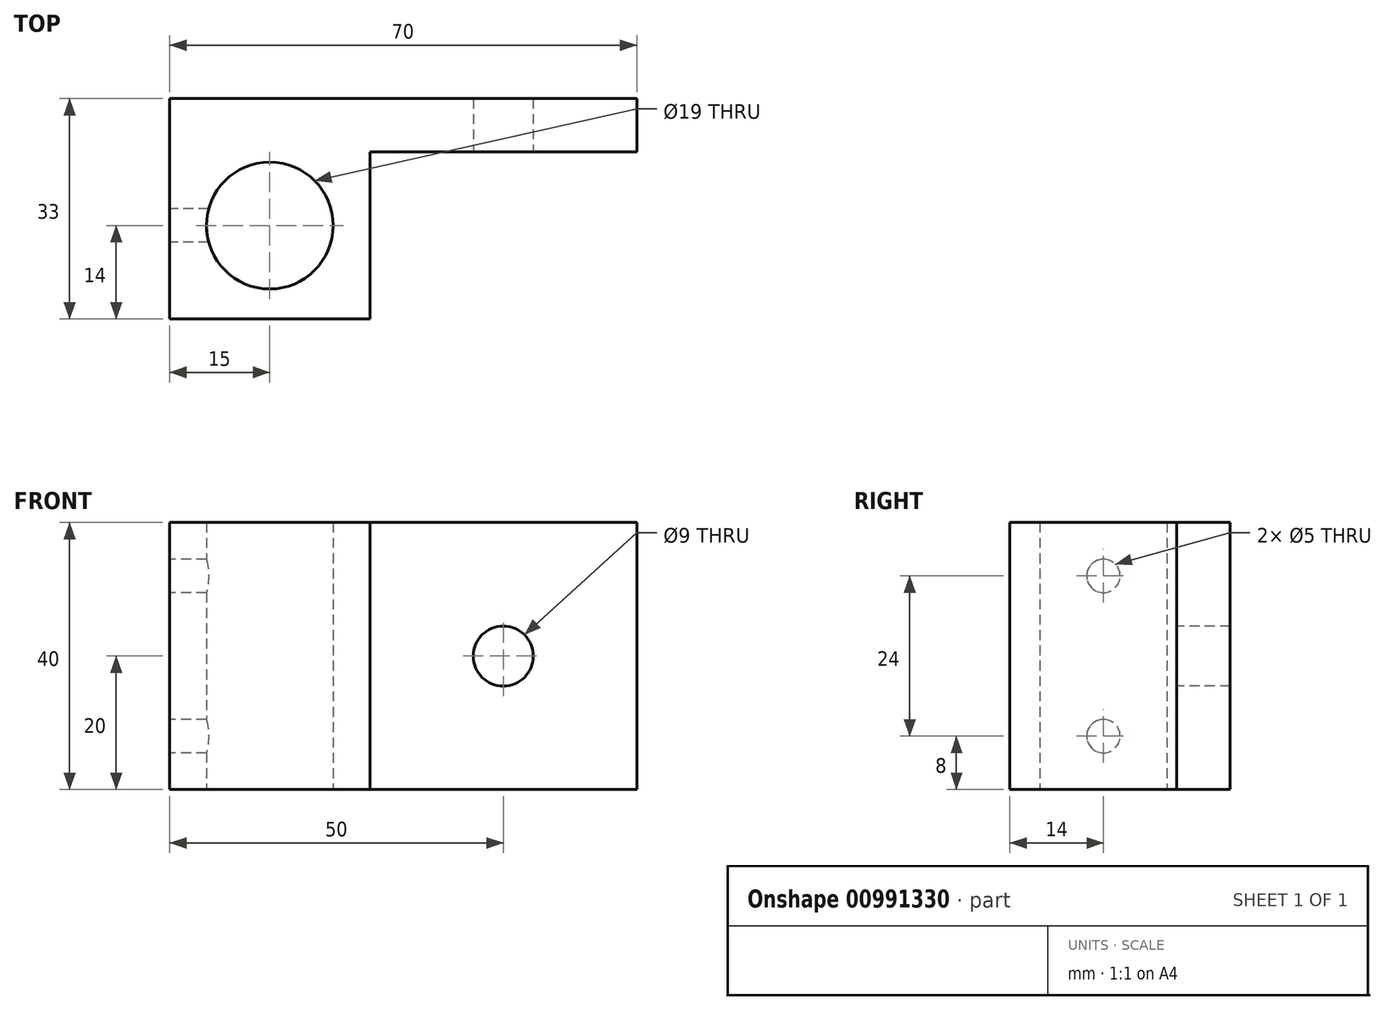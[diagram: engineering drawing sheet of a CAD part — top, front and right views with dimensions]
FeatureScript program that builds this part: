
annotation { "Feature Type Name" : "Feature", "Feature Type Description" : "" }
export const myFeature = defineFeature(function(context is Context, id is Id, definition is map)
    precondition{}
    {
        {
            var Q0;
            Q0=qCreatedBy(makeId("Front.planeOp"),FACE);
            var sketch = newSketch(context, id + "F0", { "sketchPlane" : qUnion([Q0])});
            skLineSegment(sketch, "E0.bottom", {"start": v(0, 0) * mm, "end": v(70, 0) * mm});
            skLineSegment(sketch, "E0.top", {"start": v(0, 40) * mm, "end": v(70, 40) * mm});
            skLineSegment(sketch, "E0.left", {"start": v(0, 0) * mm, "end": v(0, 40) * mm});
            skLineSegment(sketch, "E0.right", {"start": v(70, 0) * mm, "end": v(70, 40) * mm});
            skSolve(sketch);
        }
        {
            var Q0;
            Q0=makeQuery(id+"F0.imprint","IMPRINT",FACE,{"disambiguationData":[TD([[makeQuery(id+"F0.imprint","IMPRINT",EDGE,{"derivedFrom":sQuery(id+"F0.wireOp",EDGE,"E0.bottom")}),1.0]])]});
            extrude(context, id + "F1", {"entities" : qUnion([Q0]), "depth" : 8 * mm, "offsetDistance" : 25 * mm});
        }
        {
            var Q0;
            Q0=makeQuery(id+"F1.opExtrude","CAP_FACE",FACE,{"disambiguationData":[OSD([sQuery(id+"F0.wireOp",EDGE,"E0.bottom"),sQuery(id+"F0.wireOp",EDGE,"E0.top"),sQuery(id+"F0.wireOp",EDGE,"E0.left"),sQuery(id+"F0.wireOp",EDGE,"E0.right")])],"isStart":false});
            var sketch = newSketch(context, id + "F2", { "sketchPlane" : qUnion([Q0])});
            skLineSegment(sketch, "E1.bottom", {"start": v(0, 0) * mm, "end": v(30, 0) * mm});
            skLineSegment(sketch, "E1.top", {"start": v(0, 40) * mm, "end": v(30, 40) * mm});
            skLineSegment(sketch, "E1.left", {"start": v(0, 0) * mm, "end": v(0, 40) * mm});
            skLineSegment(sketch, "E1.right", {"start": v(30, 0) * mm, "end": v(30, 40) * mm});
            skSolve(sketch);
        }
        {
            var Q0;
            Q0=makeQuery(id+"F2.imprint","IMPRINT",FACE,{"disambiguationData":[TD([[makeQuery(id+"F2.imprint","IMPRINT",EDGE,{"derivedFrom":sQuery(id+"F2.wireOp",EDGE,"E1.bottom")}),1.0]])]});
            extrude(context, id + "F3", {"entities" : qUnion([Q0]), "operationType" : NewBodyOperationType.ADD, "depth" : 25 * mm, "offsetDistance" : 25 * mm});
        }
        {
            var Q0;
            Q0=makeQuery(id+"F3.boolean.opBoolean","MERGE",FACE,{"derivedFrom":[makeQuery(id+"F1.opExtrude","SWEPT_FACE",FACE,{"disambiguationData":[OSD([sQuery(id+"F0.wireOp",EDGE,"E0.bottom")])]}),makeQuery(id+"F3.opExtrude","SWEPT_FACE",FACE,{"disambiguationData":[OSD([sQuery(id+"F2.wireOp",EDGE,"E1.bottom")])]})]});
            var sketch = newSketch(context, id + "F4", { "sketchPlane" : qUnion([Q0])});
            skPoint(sketch, "E2", {"position": v(15, 19) * mm});
            skPoint(sketch, "E2.positionSnap1", {"position": v(15, 33) * mm});
            skCircle(sketch, "E3", {"center": v(15, 19) * mm, "radius": 9.5 * mm});
            skSolve(sketch);
        }
        {
            var Q0;
            Q0=makeQuery(id+"F4.imprint","IMPRINT",FACE,{"disambiguationData":[TD([[makeQuery(id+"F4.imprint","IMPRINT",EDGE,{"derivedFrom":sQuery(id+"F4.wireOp",EDGE,"E3")}),1.0]])]});
            extrude(context, id + "F5", {"entities" : qUnion([Q0]), "operationType" : NewBodyOperationType.REMOVE, "oppositeDirection" : true, "depth" : 40 * mm, "offsetDistance" : 25 * mm});
        }
        {
            var Q0;
            Q0=makeQuery(id+"F3.boolean.opBoolean","MERGE",FACE,{"derivedFrom":[makeQuery(id+"F1.opExtrude","SWEPT_FACE",FACE,{"disambiguationData":[OSD([sQuery(id+"F0.wireOp",EDGE,"E0.left")])]}),makeQuery(id+"F3.opExtrude","SWEPT_FACE",FACE,{"disambiguationData":[OSD([sQuery(id+"F2.wireOp",EDGE,"E1.left")])]})]});
            var sketch = newSketch(context, id + "F6", { "sketchPlane" : qUnion([Q0])});
            skPoint(sketch, "E4", {"position": v(33, 20) * mm});
            skPoint(sketch, "E5", {"position": v(19, 32) * mm});
            skPoint(sketch, "E6", {"position": v(19, 8) * mm});
            skSolve(sketch);
        }
        {
            var Q0;
            Q0=sQuery(id+"F6.wireOp",VERTEX,"E5");
            var Q1;
            Q1=sQuery(id+"F6.wireOp",VERTEX,"E6");
            var Q2;
            Q2=makeQuery(id+"F1.opExtrude","SWEPT_BODY",BODY,{"disambiguationData":[OSD([sQuery(id+"F0.wireOp",EDGE,"E0.bottom"),sQuery(id+"F0.wireOp",EDGE,"E0.top"),sQuery(id+"F0.wireOp",EDGE,"E0.left"),sQuery(id+"F0.wireOp",EDGE,"E0.right")])]});
            hole(context, id + "F7", {"style" : HoleStyle.SIMPLE, "endStyle" : HoleEndStyle.BLIND, "standardTappedOrClearance" : lookupTablePath({ "standard" : "ISO", "engagement" : "75%", "pitch" : "1 mm", "size" : "M6", "type" : "Tapped" }), "standardBlindInLast" : lookupTablePath({ "standard" : "ISO", "fit" : "Normal", "engagement" : "75%", "pitch" : "1 mm", "size" : "M6", "type" : "Clearance & tapped" }), "holeDiameter" : 5 * mm, "majorDiameter" : 6 * mm, "showTappedDepth" : true, "holeDepth" : 15 * mm, "isTappedThrough" : true, "tappedDepth" : 12 * mm, "tapClearance" : 3, "startFromSketch" : true, "locations" : qUnion([Q0, Q1]), "scope" : qUnion([Q2])});
        }
        {
            var Q0;
            Q0=makeQuery(id+"F1.opExtrude","CAP_FACE",FACE,{"disambiguationData":[OSD([sQuery(id+"F0.wireOp",EDGE,"E0.bottom"),sQuery(id+"F0.wireOp",EDGE,"E0.top"),sQuery(id+"F0.wireOp",EDGE,"E0.left"),sQuery(id+"F0.wireOp",EDGE,"E0.right")])],"isStart":false});
            var sketch = newSketch(context, id + "F8", { "sketchPlane" : qUnion([Q0])});
            skPoint(sketch, "E7", {"position": v(50, 20) * mm});
            skPoint(sketch, "E7.positionSnap0", {"position": v(50, 40) * mm});
            skPoint(sketch, "E7.positionSnap1", {"position": v(70, 20) * mm});
            skSolve(sketch);
        }
        {
            var Q0;
            Q0=sQuery(id+"F8.wireOp",VERTEX,"E7");
            var Q1;
            Q1=makeQuery(id+"F1.opExtrude","SWEPT_BODY",BODY,{"disambiguationData":[OSD([sQuery(id+"F0.wireOp",EDGE,"E0.bottom"),sQuery(id+"F0.wireOp",EDGE,"E0.top"),sQuery(id+"F0.wireOp",EDGE,"E0.left"),sQuery(id+"F0.wireOp",EDGE,"E0.right")])]});
            hole(context, id + "F9", {"style" : HoleStyle.SIMPLE, "endStyle" : HoleEndStyle.BLIND, "standardTappedOrClearance" : lookupTablePath({ "fit" : "Normal", "standard" : "ISO", "size" : "M8", "type" : "Clearance" }), "standardBlindInLast" : lookupTablePath({ "fit" : "Normal", "standard" : "ISO", "engagement" : "75%", "pitch" : "1.25 mm", "size" : "M8", "type" : "Clearance & tapped" }), "holeDiameter" : 9 * mm, "majorDiameter" : 6 * mm, "holeDepth" : 15 * mm, "isTappedThrough" : true, "tappedDepth" : 12 * mm, "tapClearance" : 3, "startFromSketch" : true, "locations" : qUnion([Q0]), "scope" : qUnion([Q1])});
        }
    });
